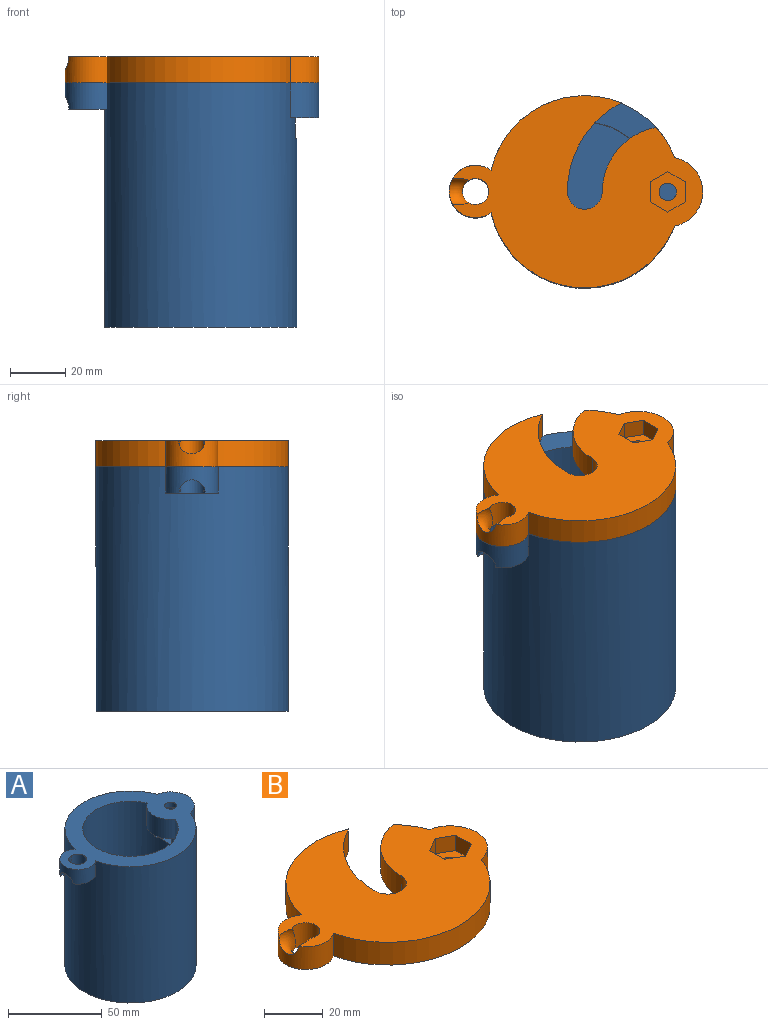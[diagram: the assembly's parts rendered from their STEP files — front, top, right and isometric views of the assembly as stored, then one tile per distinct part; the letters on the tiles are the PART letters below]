
ASSEMBLY  parts=2 mates=1
PART A: 23 faces, bbox 92.1x69.9x88.9 mm
  f0: plane 13.87x9.53mm, normal (0,0,-1), area 57.3mm2, adj f5,f18,f19,f21
  f1: plane 24.92x10.24mm, normal (0,0,-1), area 140.9mm2, adj f5,f7,f9,f10,f13,f14
  f2: plane 21.11x9.03mm, normal (0,0,-1), area 110.4mm2, adj f4,f8,f10,f11,f12,f13
  f3: plane 50.8x50.8mm, normal (0,0,1), area 2026.8mm2, adj f4
  f4: cylinder r=25.4mm len=79.38mm, axis (0,0,-1), area 12293.3mm2, adj f2,f3,f8,f10,f13,f17,f22
  f5: cylinder r=34.92mm len=88.9mm, axis (0,0,-1), area 18939.6mm2, adj f0,f1,f6,f7,f10,f13,f17,f18
  f6: plane 69.85x69.85mm, normal (0,0,-1), area 3832mm2, adj f5
  f7: cylinder r=12.7mm len=24.92mm, axis (0,0,1), area 443.7mm2, adj f1,f5,f17
  f8: cylinder r=12.7mm len=21.11mm, axis (0,0,1), area 316.6mm2, adj f2,f4,f17
  f9: plane 9.53x6.35mm, normal (-0.87,-0.5,0), area 69.8mm2, adj f1,f10,f14,f15
  f10: plane 17.15x9.75mm, normal (0,-1,0), area 144.1mm2, adj f1,f2,f4,f5,f9,f11,f15,f22
  f11: plane 9.53x6.35mm, normal (0.87,-0.5,0), area 69.8mm2, adj f2,f10,f12,f15
  f12: plane 9.53x6.35mm, normal (0.87,0.5,0), area 69.8mm2, adj f2,f11,f13,f15
  f13: plane 17.15x9.75mm, normal (0,1,0), area 144.1mm2, adj f1,f2,f4,f5,f12,f14,f15,f22
  f14: plane 9.53x6.35mm, normal (-0.87,0.5,0), area 69.8mm2, adj f1,f9,f13,f15
  f15: plane 14.66x12.7mm, normal (0,0,-1), area 108mm2, adj f9,f10,f11,f12,f13,f14,f16
  f16: cylinder r=3.17mm len=6.35mm, axis (0,0,-1), area 63.3mm2, adj f15,f17
  f17: plane 92.08x69.85mm, normal (0,0,1), area 2205.5mm2, adj f4,f5,f7,f8,f16,f18,f19,f21
  f18: cylinder r=9.53mm len=19.05mm, axis (0,0,1), area 362.4mm2, adj f0,f5,f17,f20,f21
  f19: cylinder r=4.76mm len=9.53mm, axis (0,0,1), area 157.9mm2, adj f0,f17,f20,f21
  f20: plane 13.87x9.53mm, normal (0,0,-1), area 57.3mm2, adj f5,f18,f19,f21
  f21: torus R=9.53mm, axis (0,-1,0), area 167.4mm2, adj f0,f17,f18,f19,f20
  f22: plane 12.7x10.33mm, normal (0,0,1), area 121.9mm2, adj f4,f5,f10,f13
PART B: 20 faces, bbox 92.1x69.9x14 mm
  f0: cylinder r=9.53mm len=19.05mm, axis (0,0,-1), area 362.6mm2, adj f2,f3,f9,f12,f19
  f1: cylinder r=4.78mm len=9.55mm, axis (0,0,-1), area 158.3mm2, adj f2,f12,f19
  f2: plane 90.81x69.85mm, normal (0,0,1), area 3426.5mm2, adj f0,f1,f3,f4,f5,f6,f7,f8
  f3: cylinder r=34.92mm len=66.7mm, axis (0,0,-1), area 850mm2, adj f0,f2,f4,f12
  f4: cylinder r=12.7mm len=24.92mm, axis (0,0,-1), area 332.8mm2, adj f2,f3,f5,f12
  f5: cylinder r=34.92mm len=10.97mm, axis (0,0,-1), area 123.3mm2, adj f2,f4,f6,f12
  f6: cylinder r=23.81mm len=23.43mm, axis (0,0,-1), area 315.5mm2, adj f2,f5,f7,f12
  f7: cylinder r=6.35mm len=12.7mm, axis (0,0,-1), area 190mm2, adj f2,f6,f8,f12
  f8: cylinder r=36.51mm len=32.33mm, axis (0,0,-1), area 378.3mm2, adj f2,f7,f9,f12
  f9: cylinder r=34.92mm len=47.27mm, axis (0,0,-1), area 577.7mm2, adj f0,f2,f8,f12
  f10: cylinder r=3.17mm len=6.35mm, axis (0,0,-1), area 63.3mm2, adj f11,f12
  f11: plane 14.66x12.7mm, normal (0,0,1), area 108mm2, adj f10,f13,f14,f15,f16,f17,f18
  f12: plane 92.09x69.85mm, normal (0,0,-1), area 3582.9mm2, adj f0,f1,f3,f4,f5,f6,f7,f8
  f13: plane 6.35x6.35mm, normal (-0.5,-0.87,0), area 46.6mm2, adj f2,f11,f14,f18
  f14: plane 7.33x6.35mm, normal (-1,0,0), area 46.6mm2, adj f2,f11,f13,f15
  f15: plane 6.35x6.35mm, normal (-0.5,0.87,0), area 46.6mm2, adj f2,f11,f14,f16
  f16: plane 6.35x6.35mm, normal (0.5,0.87,0), area 46.6mm2, adj f2,f11,f15,f17
  f17: plane 7.33x6.35mm, normal (1,0,0), area 46.6mm2, adj f2,f11,f16,f18
  f18: plane 6.35x6.35mm, normal (0.5,-0.87,0), area 46.6mm2, adj f2,f11,f13,f17
  f19: torus R=9.54mm, axis (0,1,0), area 167.6mm2, adj f0,f1,f2,f12
PLACE A t=(0,0,9.52)mm
PLACE B rot(axis=(0,0,-1),0.1deg) t=(0,0.06,88.9)mm
MATE revolute B.f4 <-> A.f16  axis (0,0,-1) through (30.16,0,88.9)mm
